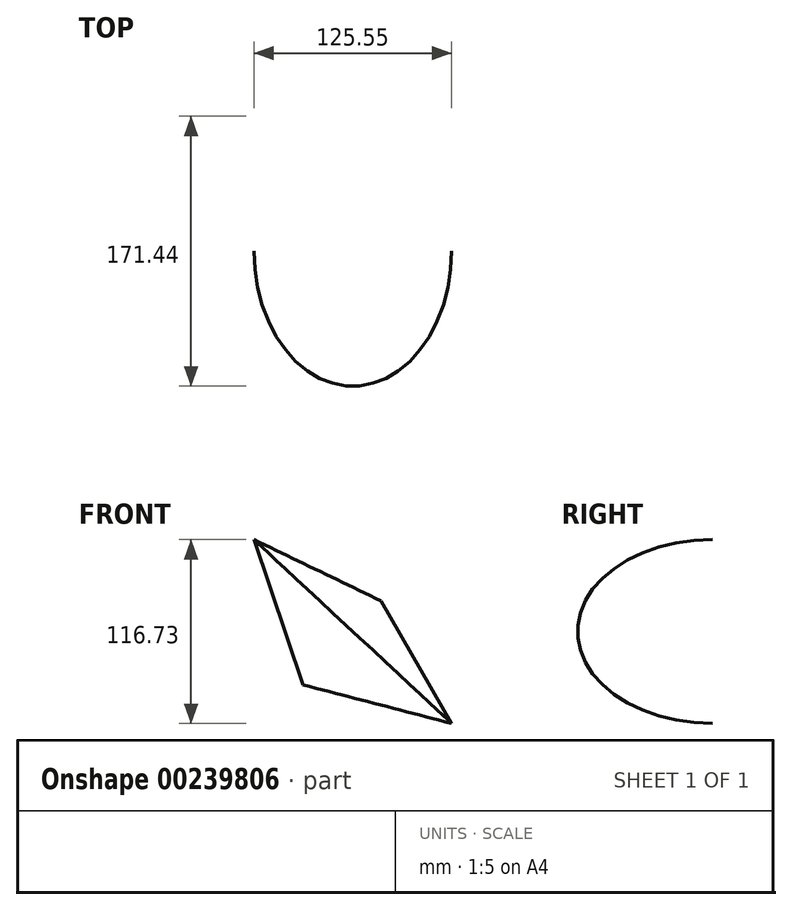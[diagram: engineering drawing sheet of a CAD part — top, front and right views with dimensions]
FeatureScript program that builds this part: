
annotation { "Feature Type Name" : "Feature", "Feature Type Description" : "" }
export const myFeature = defineFeature(function(context is Context, id is Id, definition is map)
    precondition{}
    {
        {
            var Q0;
            Q0=qCreatedBy(makeId("Front.planeOp"),FACE);
            var sketch = newSketch(context, id + "F0", { "sketchPlane" : qUnion([Q0])});
            skLineSegment(sketch, "E0", {"start": v(-50.95, 55.42) * mm, "end": v(29.84, 16.43) * mm});
            skLineSegment(sketch, "E1", {"start": v(29.84, 16.43) * mm, "end": v(-19.76, -36.9) * mm});
            skLineSegment(sketch, "E2", {"start": v(-19.76, -36.9) * mm, "end": v(-50.95, 55.42) * mm});
            skSolve(sketch);
        }
        {
            var Q0;
            Q0 = qSketchRegion(id + "F0", true);
            var Q1;
            Q1=sQuery(id+"F0.wireOp",EDGE,"E1");
            revolve(context, id + "F1", {"entities" : qUnion([Q0]), "axis" : qUnion([Q1]), "revolveType" : RevolveType.FULL});
        }
    });
